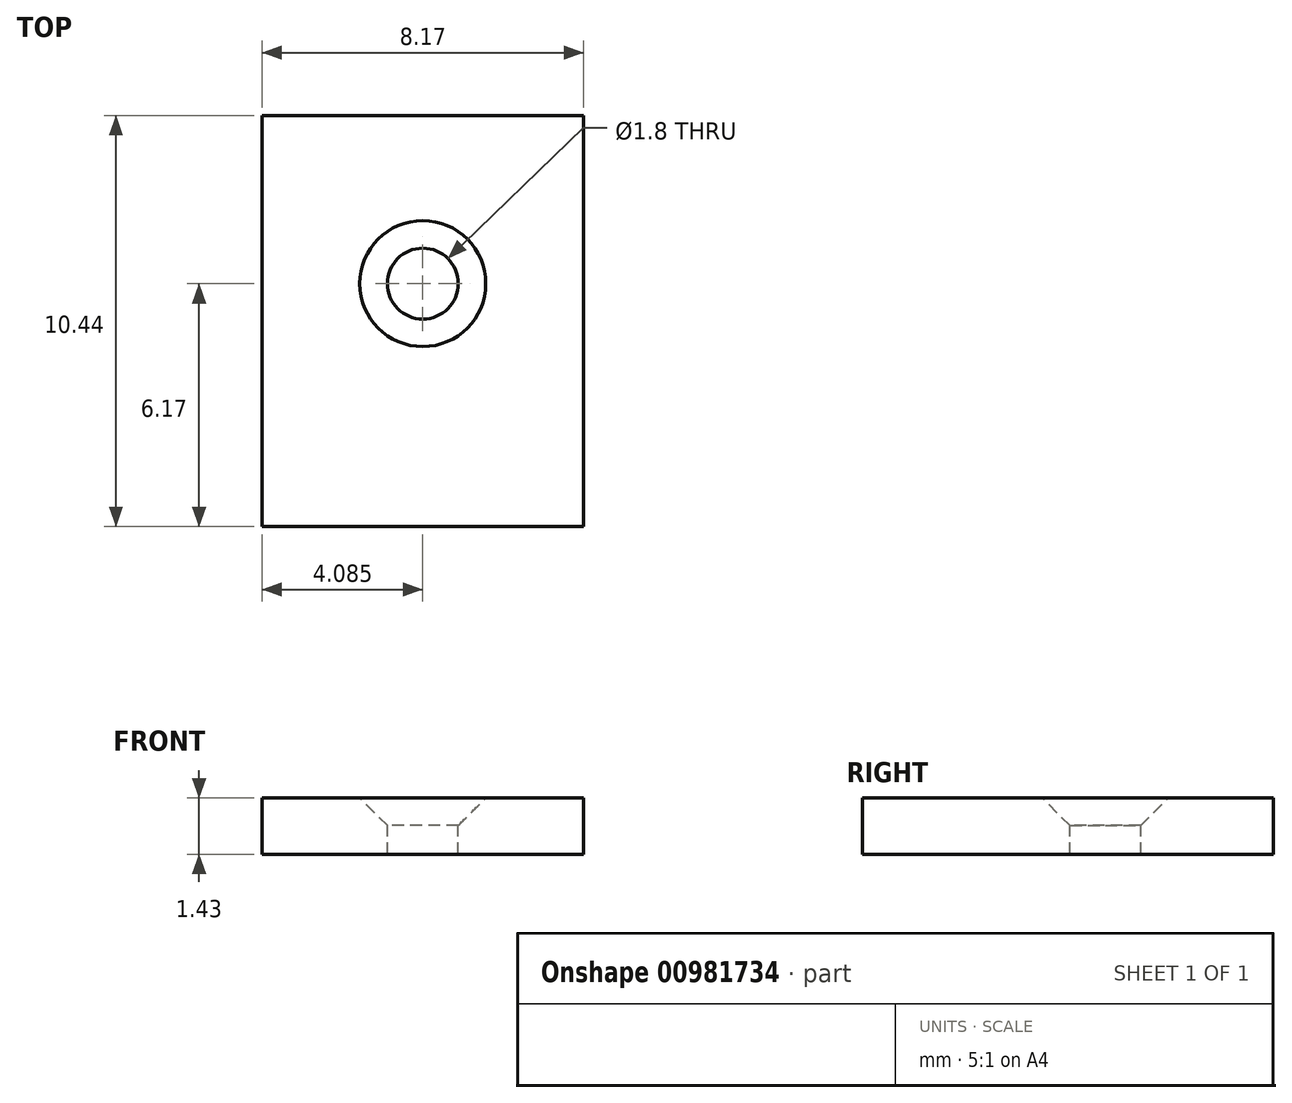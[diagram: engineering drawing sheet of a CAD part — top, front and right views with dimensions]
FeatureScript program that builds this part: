
annotation { "Feature Type Name" : "Feature", "Feature Type Description" : "" }
export const myFeature = defineFeature(function(context is Context, id is Id, definition is map)
    precondition{}
    {
        {
            var Q0;
            Q0=qCreatedBy(makeId("Top.planeOp"),FACE);
            var sketch = newSketch(context, id + "F0", { "sketchPlane" : qUnion([Q0])});
            skLineSegment(sketch, "E0.bottom", {"start": v(0, 0) * mm, "end": v(8.17, 0) * mm});
            skLineSegment(sketch, "E0.top", {"start": v(0, 10.44) * mm, "end": v(8.17, 10.44) * mm});
            skLineSegment(sketch, "E0.left", {"start": v(0, 0) * mm, "end": v(0, 10.44) * mm});
            skLineSegment(sketch, "E0.right", {"start": v(8.17, 0) * mm, "end": v(8.17, 10.44) * mm});
            skSolve(sketch);
        }
        {
            var Q0;
            Q0 = qSketchRegion(id + "F0", true);
            extrude(context, id + "F1", {"entities" : qUnion([Q0]), "depth" : 1.43 * mm, "offsetDistance" : 25 * mm});
        }
        {
            var Q0;
            Q0=makeQuery(id+"F1.opExtrude","CAP_FACE",FACE,{"disambiguationData":[OSD([sQuery(id+"F0.wireOp",EDGE,"E0.bottom"),sQuery(id+"F0.wireOp",EDGE,"E0.top"),sQuery(id+"F0.wireOp",EDGE,"E0.left"),sQuery(id+"F0.wireOp",EDGE,"E0.right")])],"isStart":false});
            var sketch = newSketch(context, id + "F2", { "sketchPlane" : qUnion([Q0])});
            skPoint(sketch, "E1", {"position": v(4.08, 6.17) * mm});
            skSolve(sketch);
        }
        {
            var Q0;
            Q0=sQuery(id+"F2.wireOp",VERTEX,"E1");
            var Q1;
            Q1=makeQuery(id+"F1.opExtrude","SWEPT_BODY",BODY,{"disambiguationData":[OSD([sQuery(id+"F0.wireOp",EDGE,"E0.bottom"),sQuery(id+"F0.wireOp",EDGE,"E0.top"),sQuery(id+"F0.wireOp",EDGE,"E0.left"),sQuery(id+"F0.wireOp",EDGE,"E0.right")])]});
            hole(context, id + "F3", {"style" : HoleStyle.C_SINK, "endStyle" : HoleEndStyle.BLIND, "standardTappedOrClearance" : lookupTablePath({ "fit" : "Normal", "standard" : "ISO", "size" : "M1.6", "type" : "Clearance" }), "standardBlindInLast" : lookupTablePath({ "fit" : "Normal", "standard" : "ISO", "engagement" : "75%", "pitch" : "0.2 mm", "size" : "M1.6", "type" : "Clearance & tapped" }), "holeDiameter" : 1.8 * mm, "cSinkDiameter" : 3.2 * mm, "cSinkAngle" : 90 * degree, "majorDiameter" : 5 * mm, "holeDepth" : 4 * mm, "isTappedThrough" : true, "tappedDepth" : 12 * mm, "tapClearance" : 3, "startFromSketch" : true, "locations" : qUnion([Q0]), "scope" : qUnion([Q1])});
        }
    });
